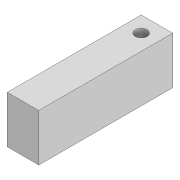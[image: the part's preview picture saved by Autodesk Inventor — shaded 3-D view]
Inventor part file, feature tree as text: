
AUTODESK INVENTOR PART (.ipt)
format: ipt  version: 2022 (Build 260153000, 153)  size: 85,504 bytes
history: native  units: mm
features: extrude x1, sketch x1
ambient origin geometry x8: Origin, YZ Plane, XZ Plane, XY Plane, X Axis, Y Axis, Z Axis, Center Point
bodies: Solid1 (feature_tree)
feature tree (2):
  extrude  "Extrusion1"  Depth=12.0mm
  sketch  "Sketch1"  dims[d0=3.0mm d1=4.0mm d2=30.0mm d3=4.0mm d4=4.0mm d5=12.0mm d6=0.0mm]
